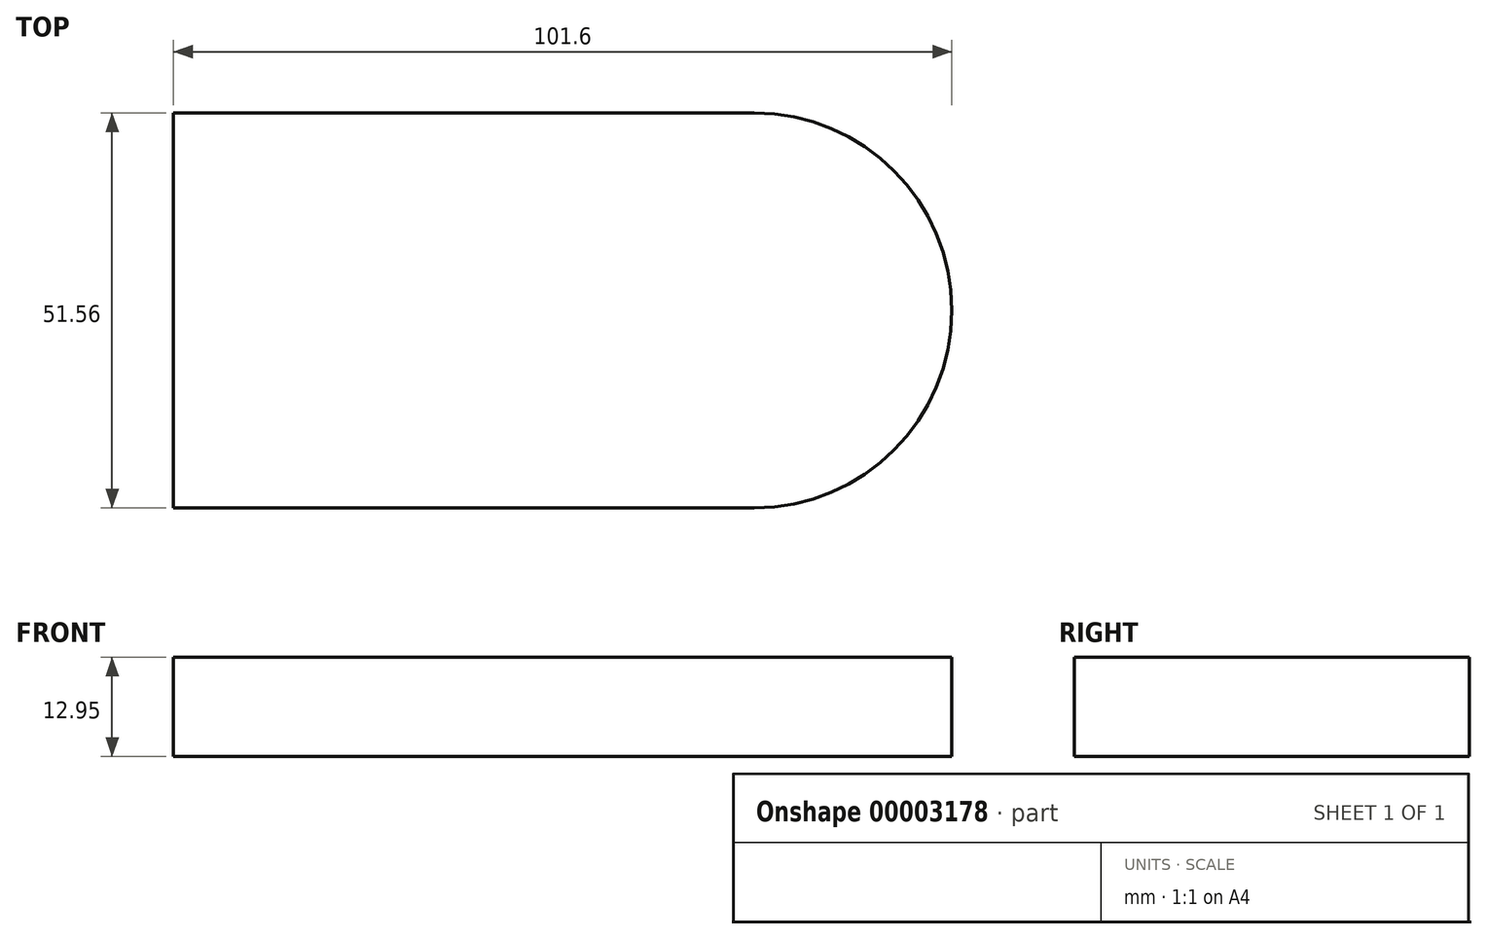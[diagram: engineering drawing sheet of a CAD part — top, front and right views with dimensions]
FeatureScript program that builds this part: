
annotation { "Feature Type Name" : "Feature", "Feature Type Description" : "" }
export const myFeature = defineFeature(function(context is Context, id is Id, definition is map)
    precondition{}
    {
        {
            var Q0;
            Q0=qCreatedBy(makeId("Top.planeOp"),FACE);
            var sketch = newSketch(context, id + "F0", { "sketchPlane" : qUnion([Q0])});
            skLineSegment(sketch, "E0.bottom", {"start": v(-25.78, 0) * mm, "end": v(-101.6, 0) * mm});
            skLineSegment(sketch, "E0.top", {"start": v(-25.78, 51.56) * mm, "end": v(-101.6, 51.56) * mm});
            skLineSegment(sketch, "E0.left", {"start": v(0, 25.78) * mm, "end": v(0, 25.78) * mm});
            skLineSegment(sketch, "E0.right", {"start": v(-101.6, 0) * mm, "end": v(-101.6, 51.56) * mm});
            skPoint(sketch, "E1.visualSharp", {"position": v(0, 0) * mm});
            skArc(sketch, "E1.filletArc", {"start": v(-25.78, 0) * mm, "mid": v(-7.55, 7.55) * mm, "end": v(0, 25.78) * mm});
            skPoint(sketch, "E2.visualSharp", {"position": v(0, 51.56) * mm});
            skArc(sketch, "E2.filletArc", {"start": v(0, 25.78) * mm, "mid": v(-7.55, 44.01) * mm, "end": v(-25.78, 51.56) * mm});
            skSolve(sketch);
        }
        {
            var Q0;
            Q0=makeQuery(id+"F0.imprint","IMPRINT",FACE,{"disambiguationData":[TD([[makeQuery(id+"F0.imprint","IMPRINT",EDGE,{"derivedFrom":sQuery(id+"F0.wireOp",EDGE,"E0.bottom")}),-1.0]])]});
            extrude(context, id + "F1", {"entities" : qUnion([Q0]), "depth" : 12.95 * mm});
        }
    });
